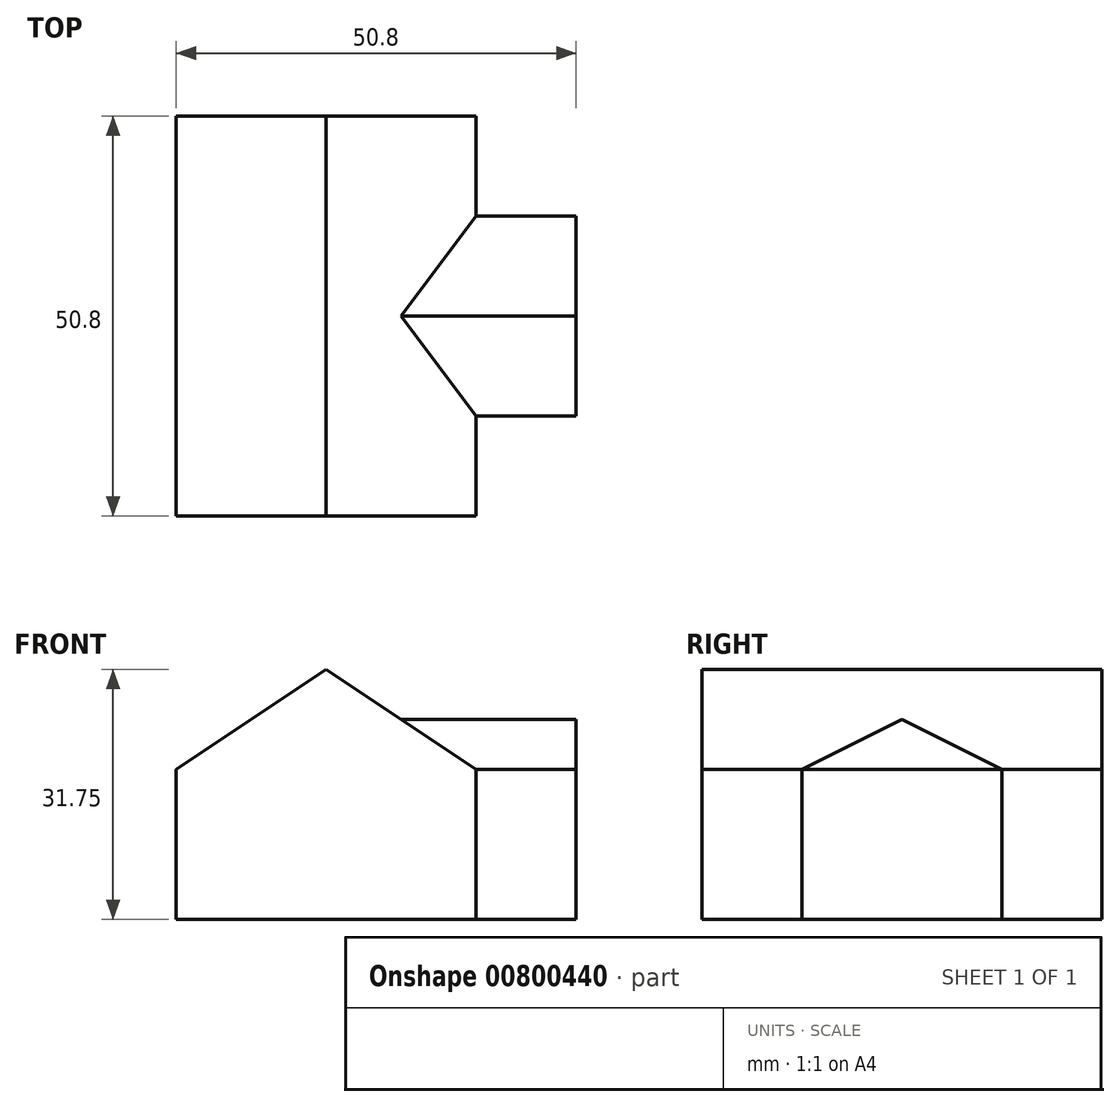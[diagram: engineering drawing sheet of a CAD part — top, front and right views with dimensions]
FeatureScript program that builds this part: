
annotation { "Feature Type Name" : "Feature", "Feature Type Description" : "" }
export const myFeature = defineFeature(function(context is Context, id is Id, definition is map)
    precondition{}
    {
        {
            var Q0;
            Q0=qCreatedBy(makeId("Front.planeOp"),FACE);
            var sketch = newSketch(context, id + "F0", { "sketchPlane" : qUnion([Q0])});
            skLineSegment(sketch, "E0", {"start": v(0, 0) * mm, "end": v(38.1, 0) * mm});
            skLineSegment(sketch, "E1", {"start": v(38.1, 0) * mm, "end": v(38.1, 19.05) * mm});
            skLineSegment(sketch, "E2", {"start": v(0, 0) * mm, "end": v(0, 19.05) * mm});
            skLineSegment(sketch, "E3", {"start": v(19.05, 0) * mm, "end": v(19.05, 31.75) * mm, "construction": true});
            skLineSegment(sketch, "E4", {"start": v(0, 19.05) * mm, "end": v(19.05, 31.75) * mm});
            skLineSegment(sketch, "E5", {"start": v(19.05, 31.75) * mm, "end": v(38.1, 19.05) * mm});
            skLineSegment(sketch, "E6", {"start": v(38.1, 0) * mm, "end": v(50.8, 0) * mm});
            skLineSegment(sketch, "E7", {"start": v(50.8, 0) * mm, "end": v(50.8, 19.05) * mm});
            skLineSegment(sketch, "E8", {"start": v(50.8, 19.05) * mm, "end": v(38.1, 19.05) * mm});
            skSolve(sketch);
        }
        {
            var Q0;
            Q0 = qSketchRegion(id + "F0", true);
            extrude(context, id + "F1", {"entities" : qUnion([Q0]), "depth" : 50.8 * mm, "offsetDistance" : 25.4 * mm});
        }
        {
            var Q0;
            Q0=makeQuery(id+"F1.opExtrude","CAP_FACE",FACE,{"disambiguationData":[OSD([sQuery(id+"F0.wireOp",EDGE,"E0"),sQuery(id+"F0.wireOp",EDGE,"E2"),sQuery(id+"F0.wireOp",EDGE,"E4"),sQuery(id+"F0.wireOp",EDGE,"E5"),sQuery(id+"F0.wireOp",EDGE,"E6"),sQuery(id+"F0.wireOp",EDGE,"E7"),sQuery(id+"F0.wireOp",EDGE,"E8")])],"isStart":false});
            var sketch = newSketch(context, id + "F2", { "sketchPlane" : qUnion([Q0])});
            skLineSegment(sketch, "E9", {"start": v(38.1, 19.05) * mm, "end": v(38.1, 0) * mm});
            skSolve(sketch);
        }
        {
            var Q0;
            {var subQ0=sQuery(id+"F2.wireOp",EDGE,"E9");Q0=makeQuery(id+"F2.imprint","IMPRINT",FACE,{"disambiguationData":[TD([[makeQuery(id+"F2.imprint","IMPRINT",EDGE,{"derivedFrom":subQ0}),1.0]])]});}
            extrude(context, id + "F3", {"entities" : qUnion([Q0]), "operationType" : NewBodyOperationType.REMOVE, "oppositeDirection" : true, "depth" : 12.7 * mm, "offsetDistance" : 25.4 * mm});
        }
        {
            var Q0;
            Q0=makeQuery(id+"F1.opExtrude","CAP_FACE",FACE,{"disambiguationData":[OSD([sQuery(id+"F0.wireOp",EDGE,"E0"),sQuery(id+"F0.wireOp",EDGE,"E2"),sQuery(id+"F0.wireOp",EDGE,"E4"),sQuery(id+"F0.wireOp",EDGE,"E5"),sQuery(id+"F0.wireOp",EDGE,"E6"),sQuery(id+"F0.wireOp",EDGE,"E7"),sQuery(id+"F0.wireOp",EDGE,"E8")])],"isStart":true});
            var sketch = newSketch(context, id + "F4", { "sketchPlane" : qUnion([Q0])});
            skLineSegment(sketch, "E10", {"start": v(-38.1, 19.05) * mm, "end": v(-38.1, 0) * mm});
            skSolve(sketch);
        }
        {
            var Q0;
            {var subQ0=sQuery(id+"F4.wireOp",EDGE,"E10");Q0=makeQuery(id+"F4.imprint","IMPRINT",FACE,{"disambiguationData":[TD([[makeQuery(id+"F4.imprint","IMPRINT",EDGE,{"derivedFrom":subQ0}),-1.0]])]});}
            extrude(context, id + "F5", {"entities" : qUnion([Q0]), "operationType" : NewBodyOperationType.REMOVE, "oppositeDirection" : true, "depth" : 12.7 * mm, "offsetDistance" : 25.4 * mm});
        }
        {
            var Q0;
            Q0=makeQuery(id+"F1.opExtrude","SWEPT_FACE",FACE,{"disambiguationData":[OSD([sQuery(id+"F0.wireOp",EDGE,"E7")])]});
            var sketch = newSketch(context, id + "F6", { "sketchPlane" : qUnion([Q0])});
            skLineSegment(sketch, "E11", {"start": v(-25.4, 0) * mm, "end": v(-25.4, 25.4) * mm, "construction": true});
            skLineSegment(sketch, "E12", {"start": v(-38.1, 19.05) * mm, "end": v(-25.4, 25.4) * mm});
            skLineSegment(sketch, "E13", {"start": v(-25.4, 25.4) * mm, "end": v(-12.7, 19.05) * mm});
            skSolve(sketch);
        }
        {
            var Q0;
            Q0=makeQuery(id+"F6.imprint","IMPRINT",FACE,{"disambiguationData":[TD([[makeQuery(id+"F6.imprint","IMPRINT",EDGE,{"derivedFrom":sQuery(id+"F6.wireOp",EDGE,"E12")}),-1.0]])]});
            extrude(context, id + "F7", {"entities" : qUnion([Q0]), "endBound" : BoundingType.UP_TO_NEXT, "oppositeDirection" : true, "depth" : 25.4 * mm, "offsetDistance" : 25.4 * mm});
        }
    });
